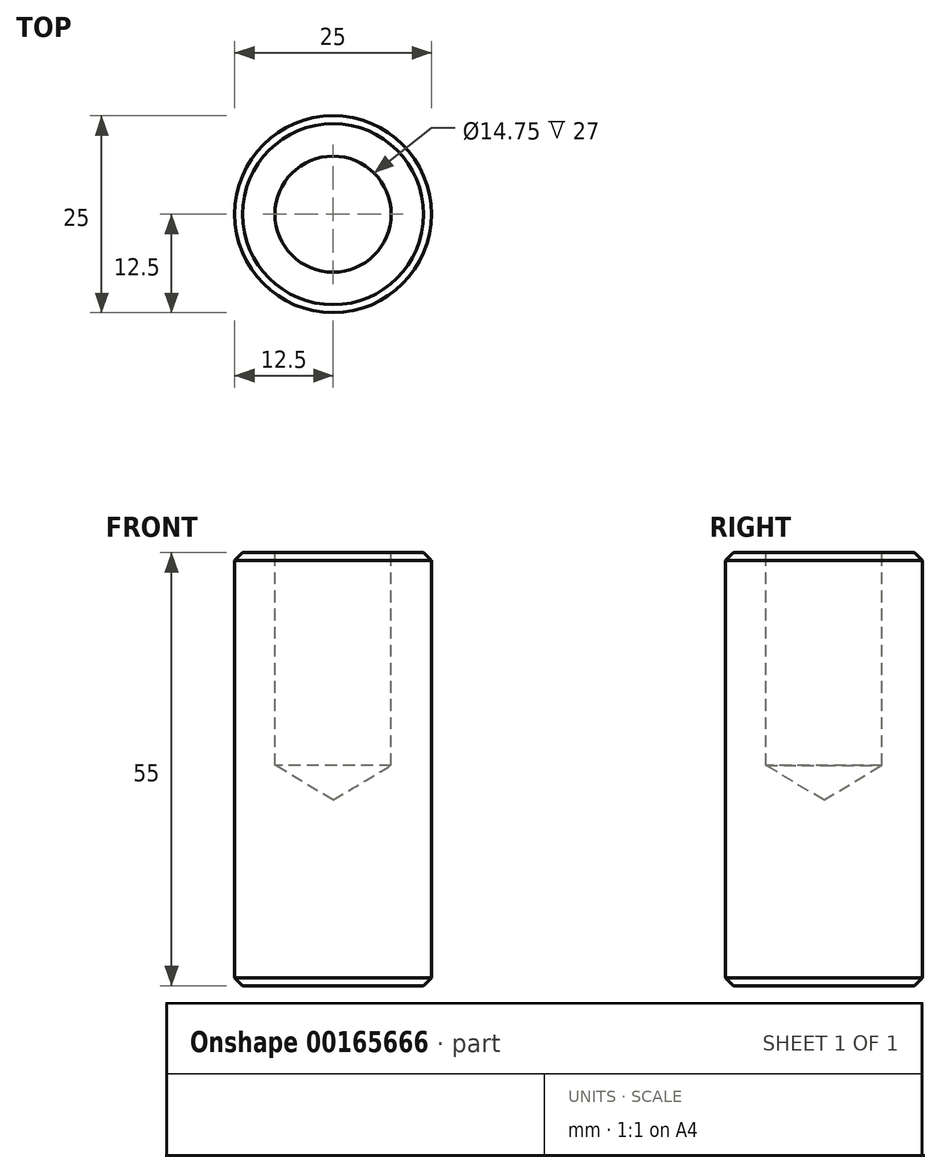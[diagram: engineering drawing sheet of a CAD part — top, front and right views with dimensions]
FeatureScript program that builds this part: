
annotation { "Feature Type Name" : "Feature", "Feature Type Description" : "" }
export const myFeature = defineFeature(function(context is Context, id is Id, definition is map)
    precondition{}
    {
        {
            var Q0;
            Q0=qCreatedBy(makeId("Top.planeOp"),FACE);
            var sketch = newSketch(context, id + "F0", { "sketchPlane" : qUnion([Q0])});
            skCircle(sketch, "E0", {"center": v(0, 0) * mm, "radius": 12.5 * mm});
            skSolve(sketch);
        }
        {
            var Q0;
            Q0=makeQuery(id+"F0.imprint","IMPRINT",FACE,{"disambiguationData":[TD([[makeQuery(id+"F0.imprint","IMPRINT",EDGE,{"derivedFrom":sQuery(id+"F0.wireOp",EDGE,"E0")}),1.0]])]});
            extrude(context, id + "F1", {"entities" : qUnion([Q0]), "depth" : 55 * mm, "offsetDistance" : 25 * mm});
        }
        {
            var Q0;
            Q0=makeQuery(id+"F1.opExtrude","CAP_EDGE",EDGE,{"disambiguationData":[OSD([sQuery(id+"F0.wireOp",EDGE,"E0")])],"isStart":true});
            var Q1;
            Q1=makeQuery(id+"F1.opExtrude","CAP_EDGE",EDGE,{"disambiguationData":[OSD([sQuery(id+"F0.wireOp",EDGE,"E0")])],"isStart":false});
            chamfer(context, id + "F2", {"entities" : qUnion([Q0, Q1]), "width" : 1 * mm, "tangentPropagation" : true});
        }
        {
            var Q0;
            Q0=makeQuery(id+"F1.opExtrude","CAP_FACE",FACE,{"disambiguationData":[OSD([sQuery(id+"F0.wireOp",EDGE,"E0")])],"isStart":false});
            var sketch = newSketch(context, id + "F3", { "sketchPlane" : qUnion([Q0]) });
            skPoint(sketch, "E1", {"position": v(0, 0) * mm});
            skSolve(sketch);
        }
        {
            var Q0;
            Q0=sQuery(id+"F3.wireOp",VERTEX,"E1");
            var Q1;
            Q1=makeQuery(id+"F1.opExtrude","SWEPT_BODY",BODY,{"disambiguationData":[OSD([sQuery(id+"F0.wireOp",EDGE,"E0")])]});
            hole(context, id + "F4", {"style" : HoleStyle.SIMPLE, "endStyle" : HoleEndStyle.BLIND, "standardTappedOrClearance" : lookupTablePath({ "standard" : "ISO", "engagement" : "50%", "pitch" : "2 mm", "size" : "M16", "type" : "Tapped" }), "standardBlindInLast" : lookupTablePath({ "standard" : "ISO", "fit" : "Normal", "engagement" : "50%", "pitch" : "2 mm", "size" : "M16", "type" : "Clearance & tapped" }), "holeDiameter" : 14.75 * mm, "majorDiameter" : 16 * mm, "showTappedDepth" : true, "holeDepth" : 27 * mm, "isTappedThrough" : true, "tappedDepth" : 27 * mm, "tapClearance" : 0, "startFromSketch" : true, "locations" : qUnion([Q0]), "scope" : qUnion([Q1])});
        }
    });
